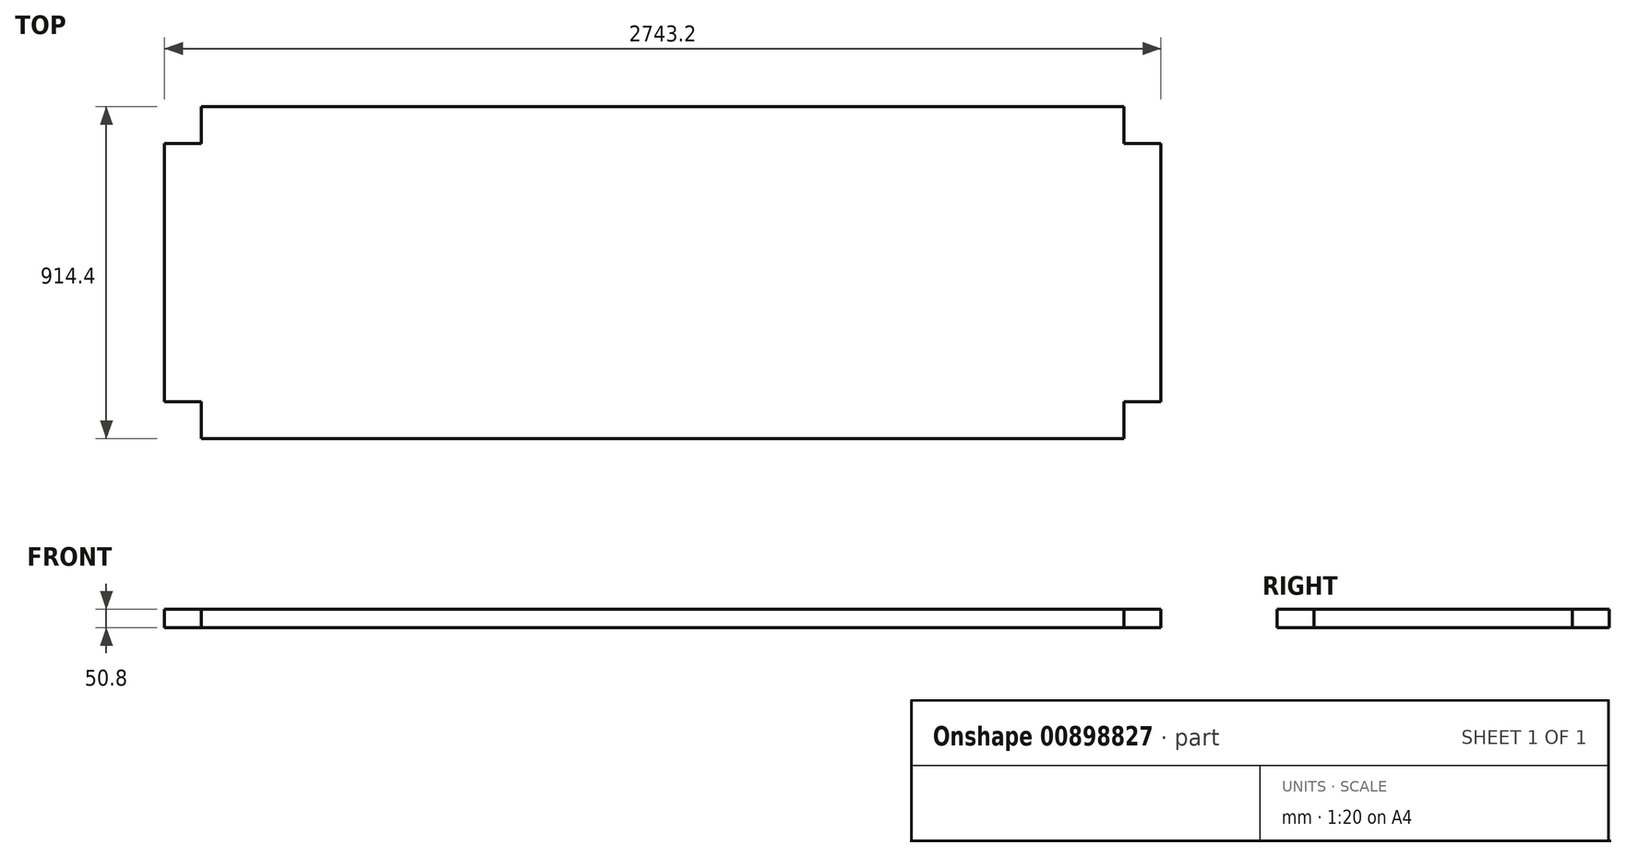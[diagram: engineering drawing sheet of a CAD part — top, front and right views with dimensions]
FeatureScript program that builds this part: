
annotation { "Feature Type Name" : "Feature", "Feature Type Description" : "" }
export const myFeature = defineFeature(function(context is Context, id is Id, definition is map)
    precondition{}
    {
        {
            var Q0;
            Q0=qCreatedBy(makeId("Top.planeOp"),FACE);
            var sketch = newSketch(context, id + "F0", { "sketchPlane" : qUnion([Q0])});
            skLineSegment(sketch, "E0.bottom", {"start": v(-1270, 457.2) * mm, "end": v(1270, 457.2) * mm});
            skLineSegment(sketch, "E0.top", {"start": v(-1270, -457.2) * mm, "end": v(1270, -457.2) * mm});
            skLineSegment(sketch, "E0.left", {"start": v(-1371.6, 355.6) * mm, "end": v(-1371.6, -355.6) * mm});
            skLineSegment(sketch, "E0.right", {"start": v(1371.6, 355.6) * mm, "end": v(1371.6, -355.6) * mm});
            skLineSegment(sketch, "E1", {"start": v(0, 0) * mm, "end": v(0, 457.2) * mm, "construction": true});
            skLineSegment(sketch, "E2", {"start": v(0, 0) * mm, "end": v(1371.6, 0) * mm, "construction": true});
            skLineSegment(sketch, "E3.top", {"start": v(-1371.6, 355.6) * mm, "end": v(-1270, 355.6) * mm});
            skLineSegment(sketch, "E3.right", {"start": v(-1270, 457.2) * mm, "end": v(-1270, 355.6) * mm});
            skLineSegment(sketch, "E4.top", {"start": v(-1371.6, -355.6) * mm, "end": v(-1270, -355.6) * mm});
            skLineSegment(sketch, "E4.right", {"start": v(-1270, -457.2) * mm, "end": v(-1270, -355.6) * mm});
            skLineSegment(sketch, "E5.top", {"start": v(1371.6, -355.6) * mm, "end": v(1270, -355.6) * mm});
            skLineSegment(sketch, "E5.right", {"start": v(1270, -457.2) * mm, "end": v(1270, -355.6) * mm});
            skLineSegment(sketch, "E6.top", {"start": v(1371.6, 355.6) * mm, "end": v(1270, 355.6) * mm});
            skLineSegment(sketch, "E6.right", {"start": v(1270, 457.2) * mm, "end": v(1270, 355.6) * mm});
            skLineSegment(sketch, "E7", {"start": v(-1270, 355.6) * mm, "end": v(-1270, -355.6) * mm, "construction": true});
            skLineSegment(sketch, "E8", {"start": v(-1270, -355.6) * mm, "end": v(1270, -355.6) * mm, "construction": true});
            skLineSegment(sketch, "E9", {"start": v(1270, -355.6) * mm, "end": v(1270, 355.6) * mm, "construction": true});
            skLineSegment(sketch, "E10", {"start": v(1270, 355.6) * mm, "end": v(-1270, 355.6) * mm, "construction": true});
            skPoint(sketch, "E11.orphan", {"position": v(-1371.6, 457.2) * mm});
            skPoint(sketch, "E12.orphan", {"position": v(1371.6, 457.2) * mm});
            skPoint(sketch, "E13.orphan", {"position": v(1371.6, -457.2) * mm});
            skSolve(sketch);
        }
        {
            var Q0;
            Q0 = qSketchRegion(id + "F0", true);
            extrude(context, id + "F1", {"entities" : qUnion([Q0]), "depth" : 50.8 * mm, "offsetDistance" : 25.4 * mm});
        }
    });
